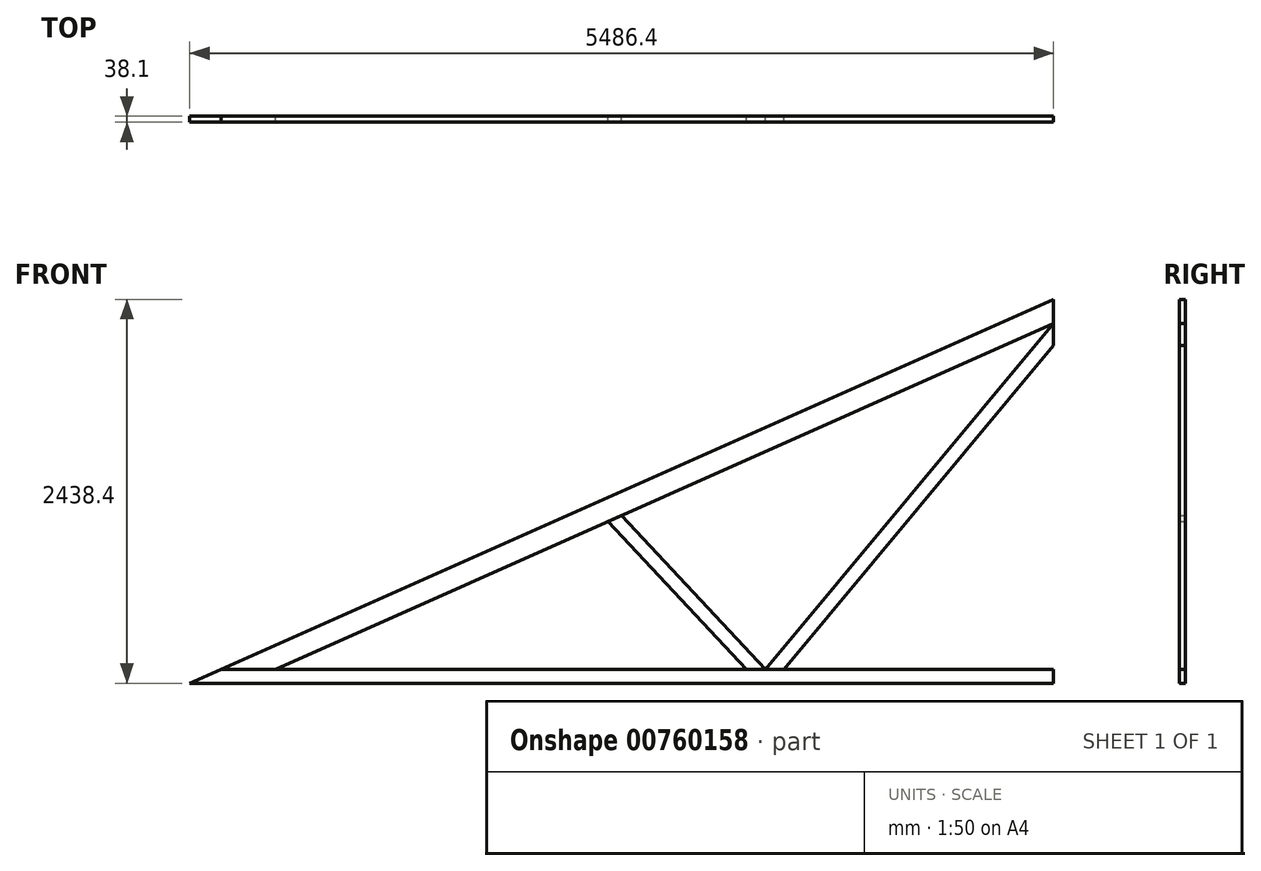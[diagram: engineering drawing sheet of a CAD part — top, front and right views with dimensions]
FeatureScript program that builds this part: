
annotation { "Feature Type Name" : "Feature", "Feature Type Description" : "" }
export const myFeature = defineFeature(function(context is Context, id is Id, definition is map)
    precondition{}
    {
        {
            var Q0;
            Q0=qCreatedBy(makeId("Front.planeOp"),FACE);
            var sketch = newSketch(context, id + "F0", { "sketchPlane" : qUnion([Q0])});
            skLineSegment(sketch, "E0", {"start": v(0, 0) * mm, "end": v(0, -2438.4) * mm, "construction": true});
            skLineSegment(sketch, "E1", {"start": v(0, -2438.4) * mm, "end": v(-5486.4, -2438.4) * mm});
            skLineSegment(sketch, "E2", {"start": v(0, -2438.4) * mm, "end": v(-1828.8, -2438.4) * mm, "construction": true});
            skLineSegment(sketch, "E3", {"start": v(-1828.8, -2438.4) * mm, "end": v(-2743.2, -2438.4) * mm, "construction": true});
            skLineSegment(sketch, "E4", {"start": v(-5486.4, -2438.4) * mm, "end": v(0, 0) * mm});
            skLineSegment(sketch, "E5", {"start": v(-2743.2, -2438.4) * mm, "end": v(-2743.2, -1372.08) * mm, "construction": true});
            skLineSegment(sketch, "E6", {"start": v(0, -2438.4) * mm, "end": v(0, -2349.5) * mm});
            skLineSegment(sketch, "E7", {"start": v(0, -2349.5) * mm, "end": v(-5286.38, -2349.5) * mm});
            skLineSegment(sketch, "E8.0", {"start": v(-4942.4, -2349.5) * mm, "end": v(0, -152.88) * mm});
            skLineSegment(sketch, "E9", {"start": v(-1828.8, -2438.4) * mm, "end": v(-1828.8, -2349.5) * mm, "construction": true});
            skLineSegment(sketch, "E10", {"start": v(-1828.8, -2349.5) * mm, "end": v(0, -152.88) * mm});
            skLineSegment(sketch, "E11", {"start": v(-1828.8, -2349.5) * mm, "end": v(-2743.2, -1372.08) * mm});
            skLineSegment(sketch, "E12.0", {"start": v(-1713.12, -2349.5) * mm, "end": v(0, -291.82) * mm});
            skLineSegment(sketch, "E13.0", {"start": v(-1950.54, -2349.5) * mm, "end": v(-2808.12, -1432.81) * mm});
            skLineSegment(sketch, "E14", {"start": v(-2808.12, -1432.81) * mm, "end": v(-2829.19, -1410.3) * mm});
            skLineSegment(sketch, "E15", {"start": v(0, 0) * mm, "end": v(0, -152.88) * mm});
            skLineSegment(sketch, "E16", {"start": v(0, -152.88) * mm, "end": v(0, -291.82) * mm});
            skSolve(sketch);
        }
        {
            var Q0;
            {var subQ7=sQuery(id+"F0.wireOp",EDGE,"E15");Q0=makeQuery(id+"F0.imprint","IMPRINT",FACE,{"disambiguationData":[TD([[makeQuery(id+"F0.imprint","IMPRINT",EDGE,{"derivedFrom":subQ7}),-1.0]])]});}
            extrude(context, id + "F1", {"entities" : qUnion([Q0]), "depth" : 38.1 * mm, "offsetDistance" : 25.4 * mm});
        }
        {
            var Q0;
            {var subQ0=sQuery(id+"F0.wireOp",EDGE,"E11");Q0=makeQuery(id+"F0.imprint","IMPRINT",FACE,{"disambiguationData":[TD([[makeQuery(id+"F0.imprint","IMPRINT",EDGE,{"derivedFrom":subQ0}),1.0]])]});}
            var Q1;
            Q1=makeQuery(id+"F1.opExtrude","CAP_FACE",FACE,{"disambiguationData":[OSD([sQuery(id+"F0.wireOp",EDGE,"E4"),sQuery(id+"F0.wireOp",EDGE,"E7"),sQuery(id+"F0.wireOp",EDGE,"E8.0"),sQuery(id+"F0.wireOp",EDGE,"E15")])],"isStart":false});
            extrude(context, id + "F2", {"entities" : qUnion([Q0]), "endBound" : BoundingType.UP_TO_SURFACE, "depth" : 25.4 * mm, "endBoundEntityFace" : qUnion([Q1]), "offsetDistance" : 25.4 * mm});
        }
        {
            var Q0;
            {var subQ0=sQuery(id+"F0.wireOp",EDGE,"E10");Q0=makeQuery(id+"F0.imprint","IMPRINT",FACE,{"disambiguationData":[TD([[makeQuery(id+"F0.imprint","IMPRINT",EDGE,{"derivedFrom":subQ0}),-1.0]])]});}
            var Q1;
            Q1=makeQuery(id+"F1.opExtrude","CAP_FACE",FACE,{"disambiguationData":[OSD([sQuery(id+"F0.wireOp",EDGE,"E4"),sQuery(id+"F0.wireOp",EDGE,"E7"),sQuery(id+"F0.wireOp",EDGE,"E8.0"),sQuery(id+"F0.wireOp",EDGE,"E15")])],"isStart":false});
            extrude(context, id + "F3", {"entities" : qUnion([Q0]), "endBound" : BoundingType.UP_TO_SURFACE, "depth" : 25.4 * mm, "endBoundEntityFace" : qUnion([Q1]), "offsetDistance" : 25.4 * mm});
        }
        {
            var Q0;
            {var subQ4=sQuery(id+"F0.wireOp",EDGE,"E1");Q0=makeQuery(id+"F0.imprint","IMPRINT",FACE,{"disambiguationData":[TD([[makeQuery(id+"F0.imprint","IMPRINT",EDGE,{"derivedFrom":subQ4}),-1.0]])]});}
            var Q1;
            Q1=makeQuery(id+"F1.opExtrude","CAP_FACE",FACE,{"disambiguationData":[OSD([sQuery(id+"F0.wireOp",EDGE,"E4"),sQuery(id+"F0.wireOp",EDGE,"E7"),sQuery(id+"F0.wireOp",EDGE,"E8.0"),sQuery(id+"F0.wireOp",EDGE,"E15")])],"isStart":false});
            extrude(context, id + "F4", {"entities" : qUnion([Q0]), "endBound" : BoundingType.UP_TO_SURFACE, "depth" : 25.4 * mm, "endBoundEntityFace" : qUnion([Q1]), "offsetDistance" : 25.4 * mm});
        }
    });
